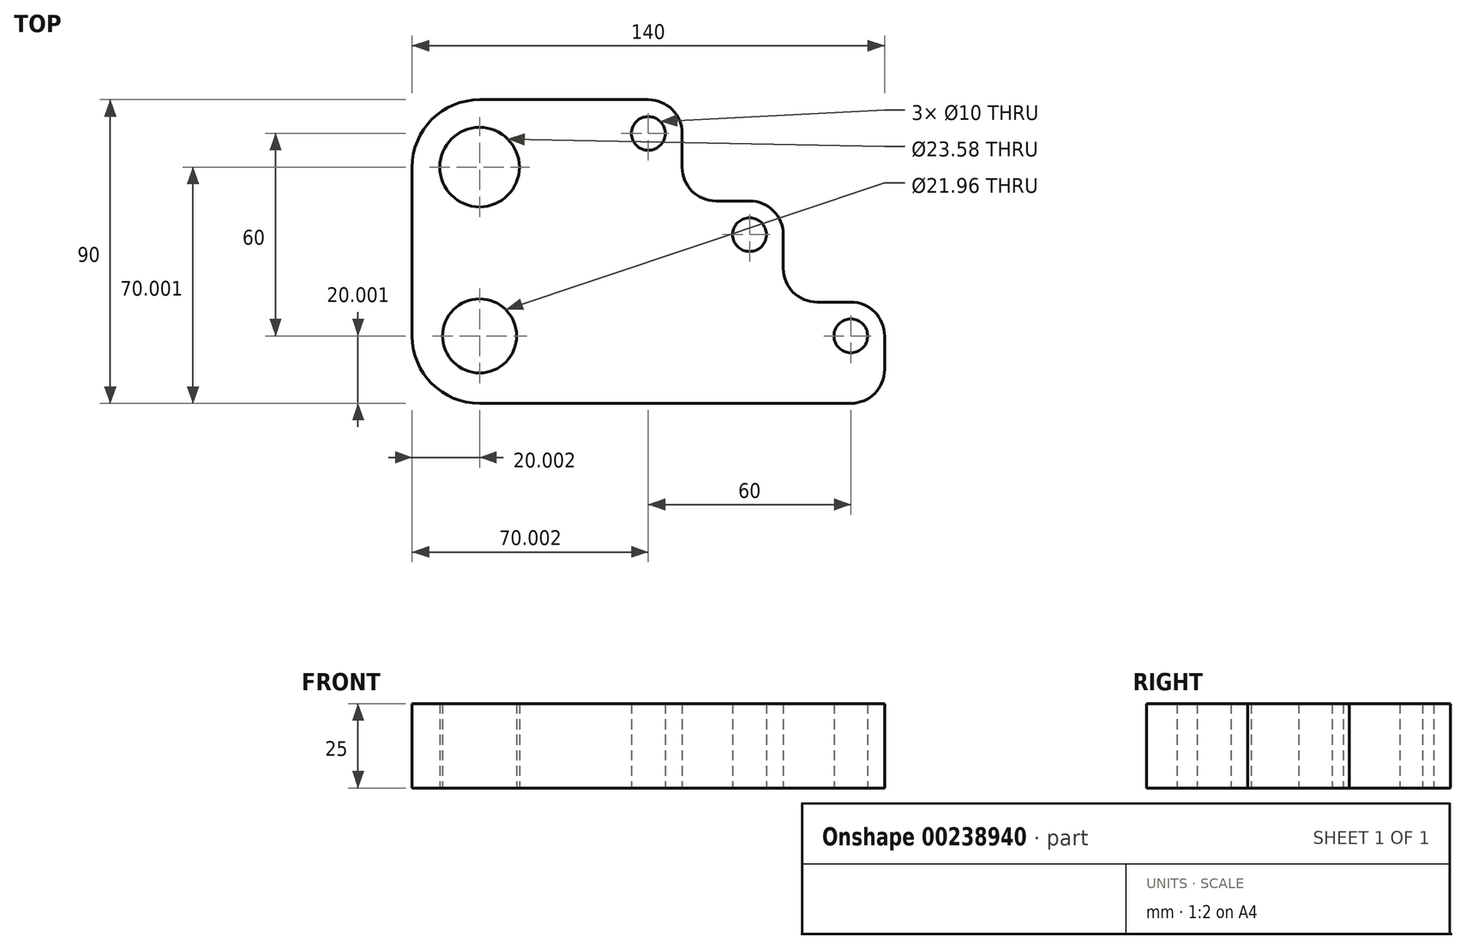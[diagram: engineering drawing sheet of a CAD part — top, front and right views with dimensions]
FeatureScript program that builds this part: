
annotation { "Feature Type Name" : "Feature", "Feature Type Description" : "" }
export const myFeature = defineFeature(function(context is Context, id is Id, definition is map)
    precondition{}
    {
        {
            var Q0;
            Q0=qCreatedBy(makeId("Top.planeOp"),FACE);
            var sketch = newSketch(context, id + "F0", { "sketchPlane" : qUnion([Q0])});
            skLineSegment(sketch, "E0", {"start": v(-39.72, -63.77) * mm, "end": v(70.28, -63.77) * mm});
            skLineSegment(sketch, "E1", {"start": v(80.28, -53.77) * mm, "end": v(80.28, -43.77) * mm});
            skLineSegment(sketch, "E2", {"start": v(70.28, -33.77) * mm, "end": v(60.28, -33.77) * mm});
            skLineSegment(sketch, "E3", {"start": v(50.28, -23.77) * mm, "end": v(50.28, -13.77) * mm});
            skLineSegment(sketch, "E4", {"start": v(40.28, -3.77) * mm, "end": v(30.28, -3.77) * mm});
            skLineSegment(sketch, "E5", {"start": v(20.28, 6.23) * mm, "end": v(20.28, 16.23) * mm});
            skLineSegment(sketch, "E6", {"start": v(-59.72, -43.77) * mm, "end": v(-59.72, 6.23) * mm});
            skLineSegment(sketch, "E7", {"start": v(-39.72, 26.23) * mm, "end": v(10.28, 26.23) * mm});
            skPoint(sketch, "E8.visualSharp", {"position": v(-59.72, 26.23) * mm});
            skArc(sketch, "E8.filletArc", {"start": v(-39.72, 26.23) * mm, "mid": v(-53.86, 20.37) * mm, "end": v(-59.72, 6.23) * mm});
            skPoint(sketch, "E9.visualSharp", {"position": v(-59.72, -63.77) * mm});
            skArc(sketch, "E9.filletArc", {"start": v(-59.72, -43.77) * mm, "mid": v(-53.86, -57.91) * mm, "end": v(-39.72, -63.77) * mm});
            skPoint(sketch, "E10.visualSharp", {"position": v(80.28, -63.77) * mm});
            skArc(sketch, "E10.filletArc", {"start": v(70.28, -63.77) * mm, "mid": v(77.35, -60.84) * mm, "end": v(80.28, -53.77) * mm});
            skPoint(sketch, "E11.visualSharp", {"position": v(80.28, -33.77) * mm});
            skArc(sketch, "E11.filletArc", {"start": v(80.28, -43.77) * mm, "mid": v(77.35, -36.7) * mm, "end": v(70.28, -33.77) * mm});
            skPoint(sketch, "E12.visualSharp", {"position": v(50.28, -33.77) * mm});
            skArc(sketch, "E12.filletArc", {"start": v(50.28, -23.77) * mm, "mid": v(53.21, -30.84) * mm, "end": v(60.28, -33.77) * mm});
            skPoint(sketch, "E13.visualSharp", {"position": v(50.28, -3.77) * mm});
            skArc(sketch, "E13.filletArc", {"start": v(50.28, -13.77) * mm, "mid": v(47.35, -6.7) * mm, "end": v(40.28, -3.77) * mm});
            skPoint(sketch, "E14.visualSharp", {"position": v(20.28, -3.77) * mm});
            skArc(sketch, "E14.filletArc", {"start": v(20.28, 6.23) * mm, "mid": v(23.21, -0.84) * mm, "end": v(30.28, -3.77) * mm});
            skPoint(sketch, "E15.visualSharp", {"position": v(20.28, 26.23) * mm});
            skArc(sketch, "E15.filletArc", {"start": v(20.28, 16.23) * mm, "mid": v(17.35, 23.3) * mm, "end": v(10.28, 26.23) * mm});
            skCircle(sketch, "E16", {"center": v(-39.72, 6.23) * mm, "radius": 11.8 * mm});
            skCircle(sketch, "E17", {"center": v(-39.72, -43.77) * mm, "radius": 10.98 * mm});
            skCircle(sketch, "E18", {"center": v(10.28, 16.23) * mm, "radius": 5 * mm});
            skCircle(sketch, "E19", {"center": v(40.28, -13.77) * mm, "radius": 5 * mm});
            skCircle(sketch, "E20", {"center": v(70.28, -43.77) * mm, "radius": 5 * mm});
            skSolve(sketch);
        }
        {
            var Q0;
            Q0=makeQuery(id+"F0.imprint","IMPRINT",FACE,{"disambiguationData":[TD([[makeQuery(id+"F0.imprint","IMPRINT",EDGE,{"derivedFrom":sQuery(id+"F0.wireOp",EDGE,"E0")}),1.0]])]});
            extrude(context, id + "F1", {"entities" : qUnion([Q0]), "depth" : 25 * mm});
        }
    });
